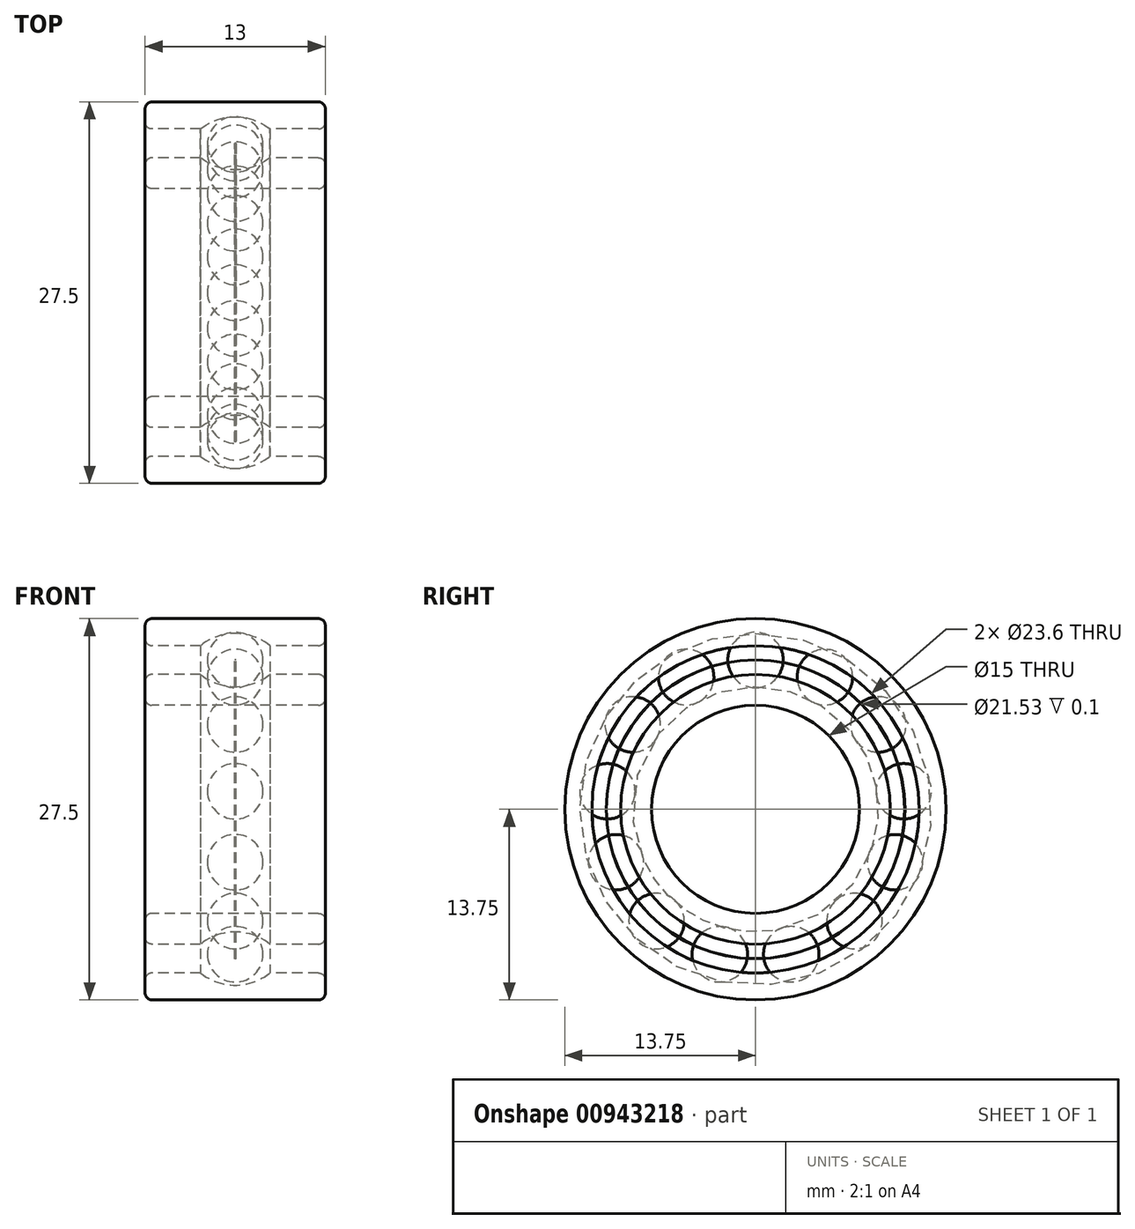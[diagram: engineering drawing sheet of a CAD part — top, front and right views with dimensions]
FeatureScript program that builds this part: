
annotation { "Feature Type Name" : "Feature", "Feature Type Description" : "" }
export const myFeature = defineFeature(function(context is Context, id is Id, definition is map)
    precondition{}
    {
        {
            var Q0;
            Q0=qCreatedBy(makeId("Front.planeOp"),FACE);
            var sketch = newSketch(context, id + "F0", { "sketchPlane" : qUnion([Q0])});
            skLineSegment(sketch, "E0", {"start": v(-6.5, 0) * mm, "end": v(6.5, 0) * mm, "construction": true});
            skLineSegment(sketch, "E1", {"start": v(-6.5, 0) * mm, "end": v(-6.5, 7.5) * mm, "construction": true});
            skLineSegment(sketch, "E2.MirrorCS", {"start": v(6.5, 0) * mm, "end": v(6.5, 7.5) * mm, "construction": true});
            skLineSegment(sketch, "E3", {"start": v(-6, 7.5) * mm, "end": v(6, 7.5) * mm});
            skLineSegment(sketch, "E4", {"start": v(-6.5, 8) * mm, "end": v(-6.5, 9.23) * mm});
            skLineSegment(sketch, "E5.MirrorCS", {"start": v(6.5, 8) * mm, "end": v(6.5, 9.23) * mm});
            skLineSegment(sketch, "E6", {"start": v(-6, 9.73) * mm, "end": v(-2.5, 9.73) * mm});
            skLineSegment(sketch, "E7.MirrorCS", {"start": v(6, 9.73) * mm, "end": v(2.5, 9.73) * mm});
            skArc(sketch, "E8", {"start": v(-2.5, 9.73) * mm, "mid": v(0, 8.85) * mm, "end": v(2.5, 9.73) * mm});
            skLineSegment(sketch, "E9", {"start": v(-6.5, 0) * mm, "end": v(-6.5, 11.8) * mm, "construction": true});
            skLineSegment(sketch, "E10", {"start": v(-6.5, 12.3) * mm, "end": v(-6.5, 13.25) * mm});
            skLineSegment(sketch, "E11", {"start": v(-6, 13.75) * mm, "end": v(0, 13.75) * mm});
            skLineSegment(sketch, "E12.MirrorCS", {"start": v(6, 13.75) * mm, "end": v(0, 13.75) * mm});
            skLineSegment(sketch, "E13.MirrorCS", {"start": v(6.5, 12.3) * mm, "end": v(6.5, 13.25) * mm});
            skLineSegment(sketch, "E14", {"start": v(-6, 11.8) * mm, "end": v(-2.5, 11.8) * mm});
            skLineSegment(sketch, "E15.MirrorCS", {"start": v(6, 11.8) * mm, "end": v(2.5, 11.8) * mm});
            skArc(sketch, "E16", {"start": v(2.5, 11.8) * mm, "mid": v(0, 12.68) * mm, "end": v(-2.5, 11.8) * mm});
            skPoint(sketch, "E17.visualSharp", {"position": v(6.5, 13.75) * mm});
            skArc(sketch, "E17.filletArc", {"start": v(6.5, 13.25) * mm, "mid": v(6.35, 13.6) * mm, "end": v(6, 13.75) * mm});
            skPoint(sketch, "E18.visualSharp", {"position": v(-6.5, 13.75) * mm});
            skArc(sketch, "E18.filletArc", {"start": v(-6, 13.75) * mm, "mid": v(-6.35, 13.6) * mm, "end": v(-6.5, 13.25) * mm});
            skPoint(sketch, "E19.visualSharp", {"position": v(-6.5, 7.5) * mm});
            skArc(sketch, "E19.filletArc", {"start": v(-6.5, 8) * mm, "mid": v(-6.35, 7.65) * mm, "end": v(-6, 7.5) * mm});
            skPoint(sketch, "E20.visualSharp", {"position": v(6.5, 7.5) * mm});
            skArc(sketch, "E20.filletArc", {"start": v(6, 7.5) * mm, "mid": v(6.35, 7.65) * mm, "end": v(6.5, 8) * mm});
            skPoint(sketch, "E21.visualSharp", {"position": v(-6.5, 11.8) * mm});
            skArc(sketch, "E21.filletArc", {"start": v(-6.5, 12.3) * mm, "mid": v(-6.35, 11.95) * mm, "end": v(-6, 11.8) * mm});
            skPoint(sketch, "E22.visualSharp", {"position": v(-6.5, 9.73) * mm});
            skArc(sketch, "E22.filletArc", {"start": v(-6, 9.73) * mm, "mid": v(-6.35, 9.58) * mm, "end": v(-6.5, 9.23) * mm});
            skPoint(sketch, "E23.visualSharp", {"position": v(6.5, 9.73) * mm});
            skArc(sketch, "E23.filletArc", {"start": v(6.5, 9.23) * mm, "mid": v(6.35, 9.58) * mm, "end": v(6, 9.73) * mm});
            skPoint(sketch, "E24.visualSharp", {"position": v(6.5, 11.8) * mm});
            skArc(sketch, "E24.filletArc", {"start": v(6, 11.8) * mm, "mid": v(6.35, 11.95) * mm, "end": v(6.5, 12.3) * mm});
            skSolve(sketch);
        }
        {
            var Q0;
            Q0=makeQuery(id+"F0.imprint","IMPRINT",FACE,{"disambiguationData":[TD([[makeQuery(id+"F0.imprint","IMPRINT",EDGE,{"derivedFrom":sQuery(id+"F0.wireOp",EDGE,"E10")}),-1.0]])]});
            var Q1;
            Q1=makeQuery(id+"F0.imprint","IMPRINT",FACE,{"disambiguationData":[TD([[makeQuery(id+"F0.imprint","IMPRINT",EDGE,{"derivedFrom":sQuery(id+"F0.wireOp",EDGE,"E3")}),1.0]])]});
            var Q2;
            Q2=sQuery(id+"F0.wireOp",EDGE,"E0");
            revolve(context, id + "F1", {"surfaceOperationType" : NewSurfaceOperationType.NEW, "entities" : qUnion([Q0, Q1]), "axis" : qUnion([Q2]), "revolveType" : RevolveType.FULL});
        }
        {
            var Q0;
            Q0=qCreatedBy(makeId("Front.planeOp"),FACE);
            var sketch = newSketch(context, id + "F2", { "sketchPlane" : qUnion([Q0])});
            skArc(sketch, "E25", {"start": v(2, 10.77) * mm, "mid": v(0, 12.76) * mm, "end": v(-2, 10.77) * mm});
            skLineSegment(sketch, "E26", {"start": v(0, 10.77) * mm, "end": v(3.74, 10.77) * mm, "construction": true});
            skLineSegment(sketch, "E27", {"start": v(0, 10.77) * mm, "end": v(0, 23.25) * mm, "construction": true});
            skLineSegment(sketch, "E28.MirrorCS", {"start": v(0, 10.77) * mm, "end": v(-3.74, 10.77) * mm, "construction": true});
            skLineSegment(sketch, "E29", {"start": v(-2, 10.77) * mm, "end": v(2, 10.77) * mm});
            skSolve(sketch);
        }
        {
            var Q0;
            Q0=qSketchRegion(id+"F2",true);
            var Q1;
            Q1=sQuery(id+"F2.wireOp",EDGE,"E28.MirrorCS");
            revolve(context, id + "F3", {"surfaceOperationType" : NewSurfaceOperationType.NEW, "entities" : qUnion([Q0]), "axis" : qUnion([Q1]), "revolveType" : RevolveType.FULL});
        }
        {
            var Q0;
            Q0=qCreatedBy(makeId("Top.planeOp"),FACE);
            var sketch = newSketch(context, id + "F4", { "sketchPlane" : qUnion([Q0])});
            skLineSegment(sketch, "E30", {"start": v(0, 0) * mm, "end": v(16.63, 0) * mm, "construction": true});
            skSolve(sketch);
        }
        {
            var Q0;
            Q0=makeQuery(id+"F3.opRevolve","SWEPT_BODY",BODY,{"disambiguationData":[OSD([sQuery(id+"F2.wireOp",EDGE,"E25"),sQuery(id+"F2.wireOp",EDGE,"E29")])]});
            var Q1;
            Q1=sQuery(id+"F4.wireOp",EDGE,"E30");
            circularPattern(context, id + "F5", {"entities" : qUnion([Q0]), "axis" : qUnion([Q1]), "angle" : 360 * degree, "instanceCount" : 13, "equalSpace" : true});
        }
        {
            var Q0;
            Q0=qCreatedBy(makeId("Right.planeOp"),FACE);
            var sketch = newSketch(context, id + "F6", { "sketchPlane" : qUnion([Q0])});
            skCircle(sketch, "E31", {"center": v(0, 0) * mm, "radius": 10.78 * mm});
            skCircle(sketch, "E32", {"center": v(0, 0) * mm, "radius": 10.77 * mm});
            skSolve(sketch);
        }
        {
            var Q0;
            Q0=qSketchRegion(id+"F6",true);
            extrude(context, id + "F7", {"entities" : qUnion([Q0]), "depth" : 0.1 * mm, "offsetDistance" : 25 * mm, "symmetric" : true});
        }
    });
